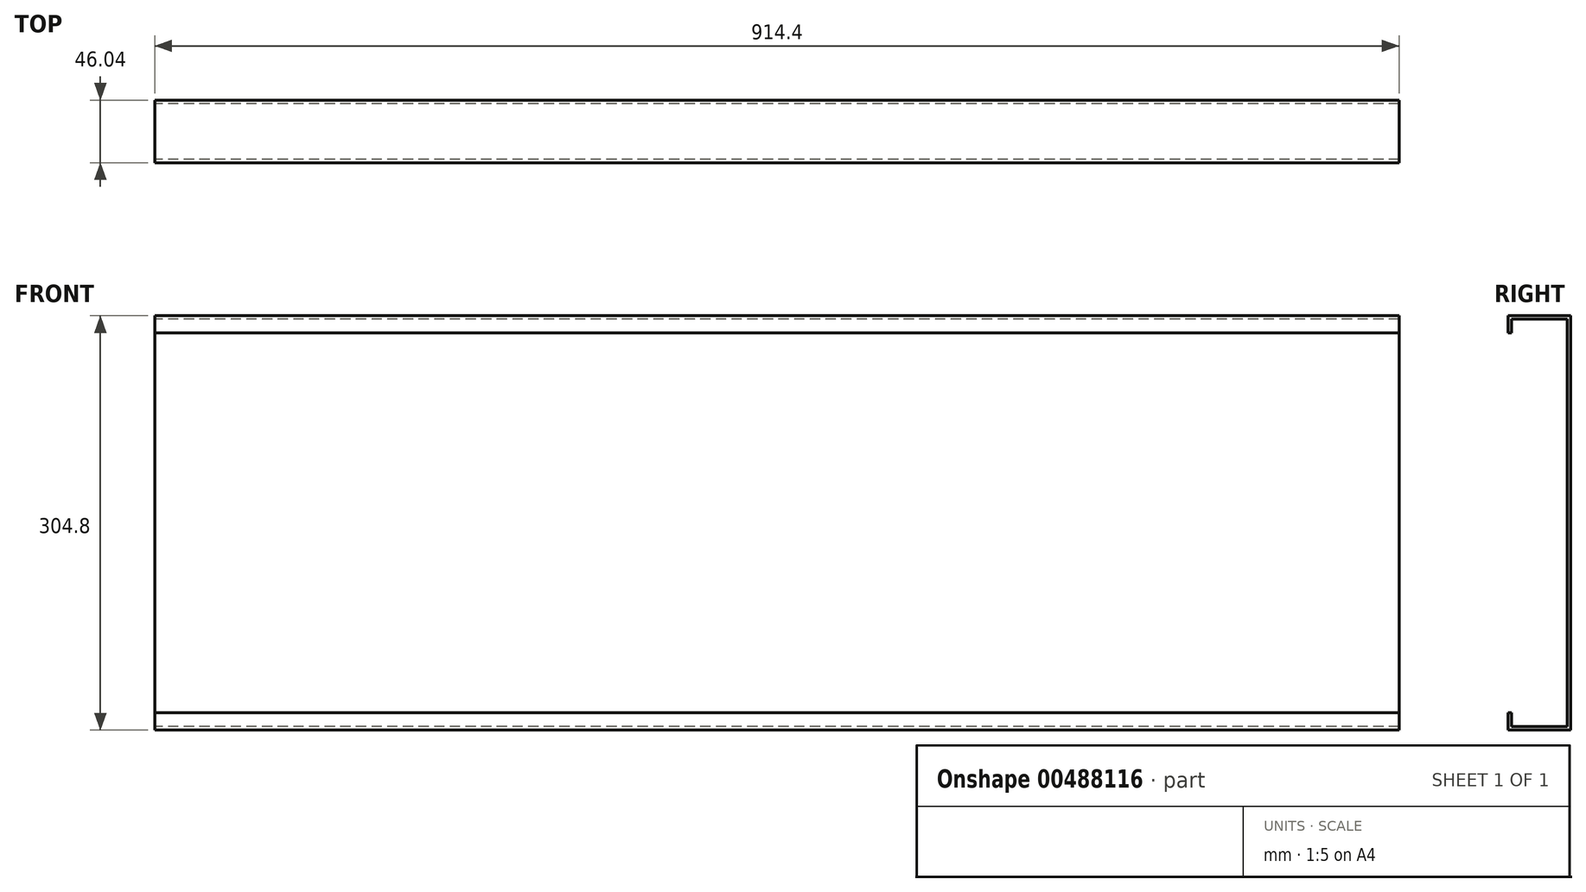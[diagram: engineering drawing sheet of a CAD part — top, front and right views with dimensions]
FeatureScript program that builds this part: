
annotation { "Feature Type Name" : "Feature", "Feature Type Description" : "" }
export const myFeature = defineFeature(function(context is Context, id is Id, definition is map)
    precondition{}
    {
        {
            var Q0;
            Q0=qCreatedBy(makeId("Right.planeOp"),FACE);
            var sketch = newSketch(context, id + "F0", { "sketchPlane" : qUnion([Q0])});
            skLineSegment(sketch, "E0", {"start": v(-23.02, 139.7) * mm, "end": v(-23.02, 152.4) * mm});
            skLineSegment(sketch, "E1", {"start": v(-23.02, 152.4) * mm, "end": v(23.02, 152.4) * mm});
            skLineSegment(sketch, "E2", {"start": v(23.02, 152.4) * mm, "end": v(23.02, -152.4) * mm});
            skLineSegment(sketch, "E3", {"start": v(23.02, -152.4) * mm, "end": v(-23.02, -152.4) * mm});
            skLineSegment(sketch, "E4", {"start": v(-23.02, -152.4) * mm, "end": v(-23.02, -139.7) * mm});
            skLineSegment(sketch, "E5.0", {"start": v(-20.48, -149.86) * mm, "end": v(-20.48, -139.7) * mm});
            skLineSegment(sketch, "E5.1", {"start": v(-20.48, 139.7) * mm, "end": v(-20.48, 149.86) * mm});
            skLineSegment(sketch, "E5.2", {"start": v(-20.48, 149.86) * mm, "end": v(20.48, 149.86) * mm});
            skLineSegment(sketch, "E5.3", {"start": v(20.48, 149.86) * mm, "end": v(20.48, -149.86) * mm});
            skLineSegment(sketch, "E5.4", {"start": v(20.48, -149.86) * mm, "end": v(-20.48, -149.86) * mm});
            skLineSegment(sketch, "E6", {"start": v(-23.02, 139.7) * mm, "end": v(-20.48, 139.7) * mm});
            skLineSegment(sketch, "E7", {"start": v(-23.02, -139.7) * mm, "end": v(-20.48, -139.7) * mm});
            skSolve(sketch);
        }
        {
            var Q0;
            Q0=makeQuery(id+"F0.imprint","IMPRINT",FACE,{"disambiguationData":[TD([[makeQuery(id+"F0.imprint","IMPRINT",EDGE,{"derivedFrom":sQuery(id+"F0.wireOp",EDGE,"E0")}),-1.0]])]});
            extrude(context, id + "F1", {"entities" : qUnion([Q0]), "depth" : 914.4 * mm});
        }
    });
